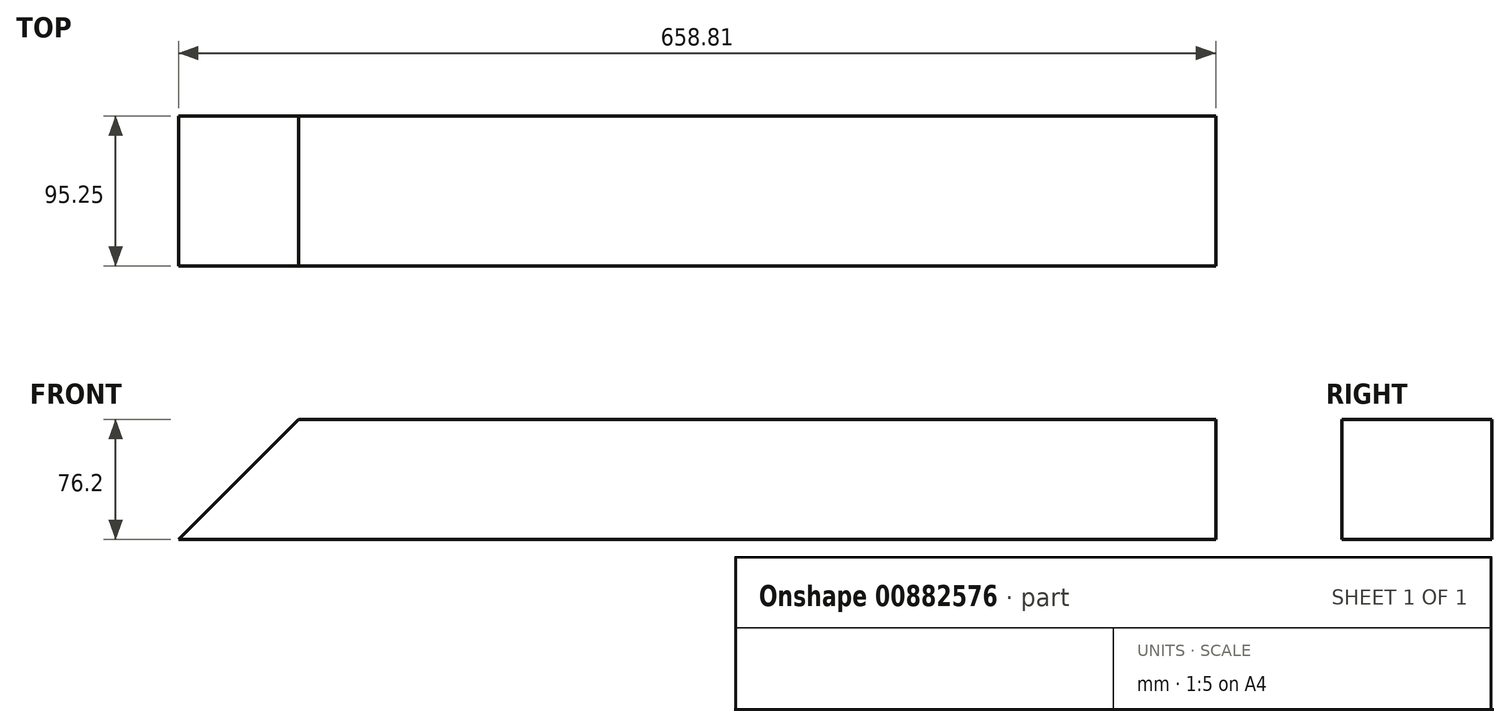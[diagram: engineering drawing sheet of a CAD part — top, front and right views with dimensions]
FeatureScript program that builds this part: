
annotation { "Feature Type Name" : "Feature", "Feature Type Description" : "" }
export const myFeature = defineFeature(function(context is Context, id is Id, definition is map)
    precondition{}
    {
        {
            var Q0;
            Q0=qCreatedBy(makeId("Right.planeOp"),FACE);
            var sketch = newSketch(context, id + "F0", { "sketchPlane" : qUnion([Q0])});
            skLineSegment(sketch, "E0.bottom", {"start": v(0, 0) * mm, "end": v(-95.25, 0) * mm});
            skLineSegment(sketch, "E0.top", {"start": v(0, -76.2) * mm, "end": v(-95.25, -76.2) * mm});
            skLineSegment(sketch, "E0.left", {"start": v(0, 0) * mm, "end": v(0, -76.2) * mm});
            skLineSegment(sketch, "E0.right", {"start": v(-95.25, 0) * mm, "end": v(-95.25, -76.2) * mm});
            skSolve(sketch);
        }
        {
            var Q0;
            Q0=makeQuery(id+"F0.imprint","IMPRINT",FACE,{"disambiguationData":[TD([[makeQuery(id+"F0.imprint","IMPRINT",EDGE,{"derivedFrom":sQuery(id+"F0.wireOp",EDGE,"E0.bottom")}),1.0]])]});
            extrude(context, id + "F1", {"entities" : qUnion([Q0]), "depth" : 658.8 * mm, "offsetDistance" : 25.4 * mm});
        }
        {
            var Q0;
            Q0=makeQuery(id+"F1.opExtrude","SWEPT_FACE",FACE,{"disambiguationData":[OSD([sQuery(id+"F0.wireOp",EDGE,"E0.right")])]});
            var sketch = newSketch(context, id + "F2", { "sketchPlane" : qUnion([Q0])});
            skLineSegment(sketch, "E1", {"start": v(0, 0) * mm, "end": v(0, -76.2) * mm});
            skLineSegment(sketch, "E2", {"start": v(0, -76.2) * mm, "end": v(76.2, 0) * mm});
            skLineSegment(sketch, "E3", {"start": v(76.2, 0) * mm, "end": v(0, 0) * mm});
            skSolve(sketch);
        }
        {
            var Q0;
            Q0=makeQuery(id+"F2.imprint","IMPRINT",FACE,{"disambiguationData":[TD([[makeQuery(id+"F2.imprint","IMPRINT",EDGE,{"derivedFrom":sQuery(id+"F2.wireOp",EDGE,"E1")}),1.0]])]});
            extrude(context, id + "F3", {"entities" : qUnion([Q0]), "operationType" : NewBodyOperationType.REMOVE, "endBound" : BoundingType.THROUGH_ALL, "oppositeDirection" : true, "depth" : 25.4 * mm, "offsetDistance" : 25.4 * mm});
        }
    });
